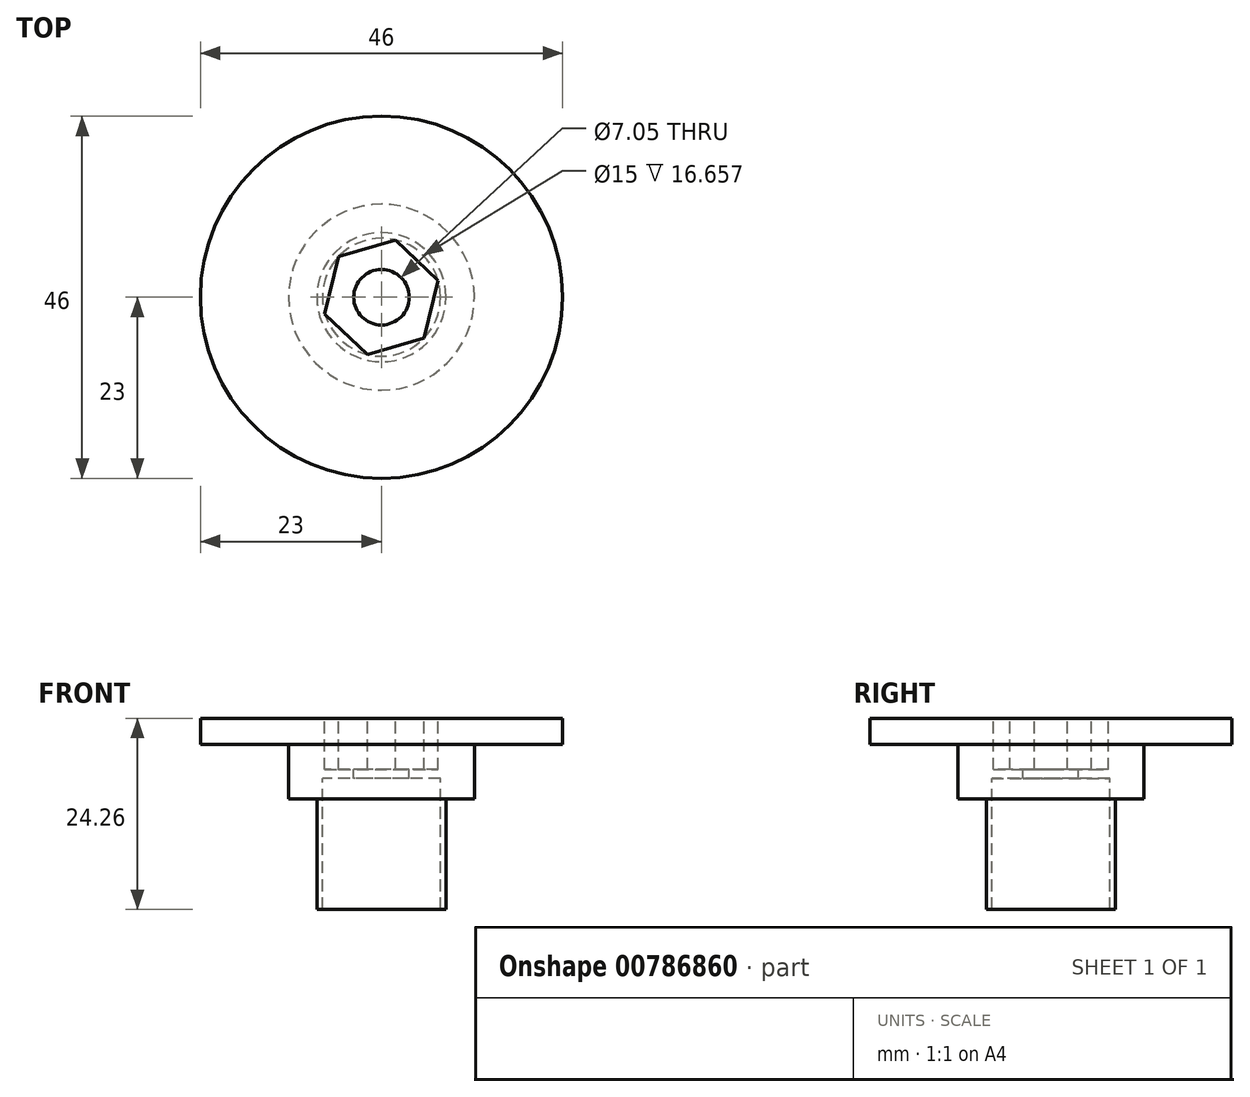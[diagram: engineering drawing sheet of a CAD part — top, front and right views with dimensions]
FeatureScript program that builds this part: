
annotation { "Feature Type Name" : "Feature", "Feature Type Description" : "" }
export const myFeature = defineFeature(function(context is Context, id is Id, definition is map)
    precondition{}
    {
        {
            var Q0;
            Q0=qCreatedBy(makeId("Front.planeOp"),FACE);
            var sketch = newSketch(context, id + "F0", { "sketchPlane" : qUnion([Q0])});
            skLineSegment(sketch, "E0.top", {"start": v(-7.5, -20) * mm, "end": v(7.5, -20) * mm, "construction": true});
            skLineSegment(sketch, "E1.0", {"start": v(-8.2, 18.3) * mm, "end": v(-8.2, 10.34) * mm});
            skLineSegment(sketch, "E2", {"start": v(-8.2, -20) * mm, "end": v(-7.5, -20) * mm});
            skLineSegment(sketch, "E3", {"start": v(-7.5, 20.7) * mm, "end": v(-7.5, 27) * mm});
            skLineSegment(sketch, "E4", {"start": v(0, 20) * mm, "end": v(0, 18.3) * mm});
            skLineSegment(sketch, "E5", {"start": v(-23, 26.95) * mm, "end": v(-23, 28.3) * mm});
            skPoint(sketch, "E6.left.start.orphan", {"position": v(-4.9, 17.77) * mm});
            skPoint(sketch, "E7.orphan", {"position": v(-4.9, 22.23) * mm});
            skPoint(sketch, "E8.orphan", {"position": v(-7.5, 20) * mm});
            skLineSegment(sketch, "E9.trimOffspring", {"start": v(-8.2, 18.3) * mm, "end": v(-11.8, 18.3) * mm});
            skPoint(sketch, "E10.orphan", {"position": v(-4.9, 20) * mm});
            skLineSegment(sketch, "E11.MirrorCS", {"start": v(8.2, -20) * mm, "end": v(7.5, -20) * mm});
            skLineSegment(sketch, "E12.MirrorCS", {"start": v(3.53, 20) * mm, "end": v(3.53, 20.7) * mm});
            skLineSegment(sketch, "E13.MirrorCS", {"start": v(7.5, 27) * mm, "end": v(7.5, 28.3) * mm});
            skLineSegment(sketch, "E14.MirrorCS", {"start": v(7.5, 20.7) * mm, "end": v(3.53, 20.7) * mm});
            skLineSegment(sketch, "E15.MirrorCS", {"start": v(3.53, 20.7) * mm, "end": v(7.5, 20.7) * mm});
            skPoint(sketch, "E16.MirrorP", {"position": v(4.9, 22.23) * mm});
            skLineSegment(sketch, "E17.MirrorCS", {"start": v(7.5, 10.34) * mm, "end": v(7.5, -20) * mm});
            skPoint(sketch, "E18.MirrorP", {"position": v(7.5, 20) * mm});
            skLineSegment(sketch, "E19.MirrorCS", {"start": v(8.2, 18.3) * mm, "end": v(23, 18.3) * mm});
            skLineSegment(sketch, "E20.MirrorCS", {"start": v(23, 28.3) * mm, "end": v(7.5, 28.3) * mm});
            skPoint(sketch, "E21.MirrorP", {"position": v(4.9, 20) * mm});
            skLineSegment(sketch, "E22.MirrorCS", {"start": v(23, 18.3) * mm, "end": v(23, 28.3) * mm});
            skPoint(sketch, "E23.MirrorP", {"position": v(4.9, 17.77) * mm});
            skLineSegment(sketch, "E24.MirrorCS", {"start": v(7.5, 20.7) * mm, "end": v(7.5, 27) * mm});
            skLineSegment(sketch, "E25.MirrorCS", {"start": v(8.2, 18.3) * mm, "end": v(8.2, -20) * mm});
            skLineSegment(sketch, "E26.MirrorCS", {"start": v(5.36, 18.3) * mm, "end": v(7.5, 10.34) * mm});
            skLineSegment(sketch, "E27.MirrorCS", {"start": v(0, 18.3) * mm, "end": v(5.36, 18.3) * mm});
            skPoint(sketch, "E28.MirrorCS.end.orphan", {"position": v(3.53, 20) * mm});
            skPoint(sketch, "E28.MirrorCS.start.orphan", {"position": v(0, 20) * mm});
            skLineSegment(sketch, "E29.top", {"start": v(-7.5, 27) * mm, "end": v(-3.53, 27) * mm});
            skLineSegment(sketch, "E29.right", {"start": v(-3.53, 28.3) * mm, "end": v(-3.53, 27) * mm});
            skLineSegment(sketch, "E30", {"start": v(-7.5, 20.7) * mm, "end": v(-7.5, 10.34) * mm});
            skPoint(sketch, "E31.end.orphan", {"position": v(-5.36, 18.3) * mm});
            skPoint(sketch, "E32.left.end.orphan", {"position": v(-3.53, 20.7) * mm});
            skPoint(sketch, "E32.left.start.orphan", {"position": v(-3.53, 20) * mm});
            skLineSegment(sketch, "E33", {"start": v(-23, 31.29) * mm, "end": v(-23, 34.6) * mm});
            skLineSegment(sketch, "E34", {"start": v(-23, 34.6) * mm, "end": v(-3.53, 34.6) * mm});
            skLineSegment(sketch, "E35.right", {"start": v(-3.53, 28.3) * mm, "end": v(-3.53, 34.6) * mm});
            skPoint(sketch, "E29.bottom.start.orphan", {"position": v(-7.5, 28.3) * mm});
            skLineSegment(sketch, "E36", {"start": v(0, 20) * mm, "end": v(0, 34.77) * mm});
            skLineSegment(sketch, "E37", {"start": v(-8.2, 18.3) * mm, "end": v(-7.5, 18.3) * mm});
            skLineSegment(sketch, "E38", {"start": v(-7.5, 10.34) * mm, "end": v(-8.2, 10.34) * mm});
            skLineSegment(sketch, "E39", {"start": v(-11.8, 24.35) * mm, "end": v(-11.8, 26.95) * mm});
            skPoint(sketch, "E40.orphan", {"position": v(-23, 18.3) * mm});
            skLineSegment(sketch, "E41", {"start": v(-8.2, 18.3) * mm, "end": v(-8.2, 24.35) * mm});
            skLineSegment(sketch, "E42", {"start": v(-8.2, 24.35) * mm, "end": v(-11.8, 24.35) * mm});
            skLineSegment(sketch, "E43", {"start": v(-11.8, 24.35) * mm, "end": v(-11.8, 31.29) * mm});
            skLineSegment(sketch, "E44", {"start": v(-11.8, 31.29) * mm, "end": v(-23, 31.29) * mm});
            skSolve(sketch);
        }
        {
            var Q0;
            Q0=makeQuery(id+"F0.imprint","IMPRINT",FACE,{"disambiguationData":[TD([[makeQuery(id+"F0.imprint","IMPRINT",EDGE,{"derivedFrom":sQuery(id+"F0.wireOp",EDGE,"E0.left")}),-1.0]])]});
            var Q1;
            {var subQ2=sQuery(id+"F0.wireOp",EDGE,"E3");Q1=makeQuery(id+"F0.imprint","IMPRINT",FACE,{"disambiguationData":[TD([[makeQuery(id+"F0.imprint","IMPRINT",EDGE,{"derivedFrom":subQ2}),1.0]])]});}
            var Q2;
            Q2=makeQuery(id+"F0.imprint","IMPRINT",FACE,{"disambiguationData":[TD([[makeQuery(id+"F0.imprint","IMPRINT",EDGE,{"derivedFrom":sQuery(id+"F0.wireOp",EDGE,"E1.0")}),1.0]])]});
            var Q3;
            Q3=sQuery(id+"F0.wireOp",EDGE,"E4");
            revolve(context, id + "F1", {"surfaceOperationType" : NewSurfaceOperationType.NEW, "entities" : qUnion([Q0, Q1, Q2]), "axis" : qUnion([Q3]), "revolveType" : RevolveType.FULL});
        }
        {
            var Q0;
            Q0=makeQuery(id+"F1.opRevolve","SWEPT_FACE",FACE,{"disambiguationData":[OSD([sQuery(id+"F0.wireOp",EDGE,"E34")])]});
            var sketch = newSketch(context, id + "F2", { "sketchPlane" : qUnion([Q0])});
            skCircle(sketch, "E45.cCircle", {"center": v(0, 0) * mm, "radius": 6.5 * mm, "construction": true});
            skLineSegment(sketch, "E45.0", {"start": v(-1.78, -7.3) * mm, "end": v(-7.2, -2.1) * mm});
            skLineSegment(sketch, "E45.1", {"start": v(-7.2, -2.1) * mm, "end": v(-5.43, 5.18) * mm});
            skLineSegment(sketch, "E45.2", {"start": v(-5.43, 5.18) * mm, "end": v(1.78, 7.3) * mm});
            skLineSegment(sketch, "E45.3", {"start": v(1.78, 7.3) * mm, "end": v(7.2, 2.1) * mm});
            skLineSegment(sketch, "E45.4", {"start": v(7.2, 2.1) * mm, "end": v(5.43, -5.18) * mm});
            skLineSegment(sketch, "E45.5", {"start": v(5.43, -5.18) * mm, "end": v(-1.78, -7.3) * mm});
            skPoint(sketch, "E45.0.midPoint", {"position": v(-4.49, -4.7) * mm});
            skSolve(sketch);
        }
        {
            var Q0;
            Q0=makeQuery(id+"F2.imprint","IMPRINT",FACE,{"disambiguationData":[TD([[makeQuery(id+"F2.imprint","IMPRINT",EDGE,{"derivedFrom":sQuery(id+"F2.wireOp",EDGE,"E45.0")}),-1.0]])]});
            extrude(context, id + "F3", {"entities" : qUnion([Q0]), "operationType" : NewBodyOperationType.REMOVE, "oppositeDirection" : true, "depth" : 6.5 * mm, "offsetDistance" : 25 * mm});
        }
    });
